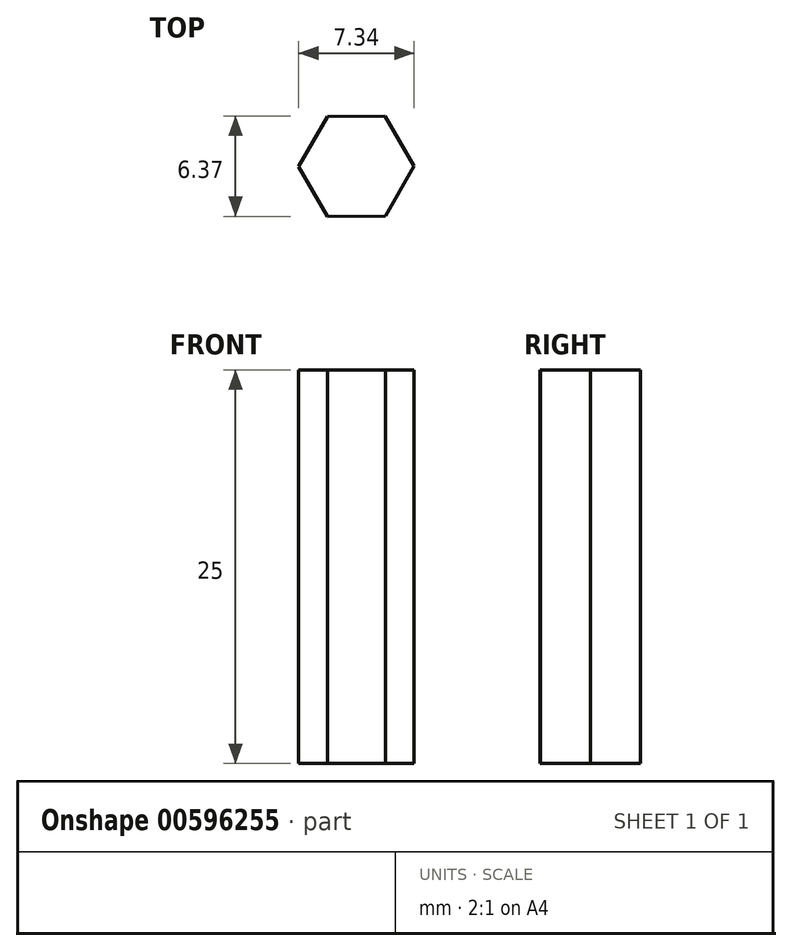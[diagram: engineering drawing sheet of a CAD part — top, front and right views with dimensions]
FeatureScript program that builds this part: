
annotation { "Feature Type Name" : "Feature", "Feature Type Description" : "" }
export const myFeature = defineFeature(function(context is Context, id is Id, definition is map)
    precondition{}
    {
        {
            var Q0;
            Q0=qCreatedBy(makeId("Top.planeOp"),FACE);
            var sketch = newSketch(context, id + "F0", { "sketchPlane" : qUnion([Q0])});
            skCircle(sketch, "E0.cCircle", {"center": v(0, 0) * mm, "radius": 3.18 * mm, "construction": true});
            skLineSegment(sketch, "E0.0", {"start": v(-1.83, -3.2) * mm, "end": v(-3.68, -0.02) * mm});
            skLineSegment(sketch, "E0.1", {"start": v(-3.68, -0.02) * mm, "end": v(-1.85, 3.16) * mm});
            skLineSegment(sketch, "E0.2", {"start": v(-1.85, 3.16) * mm, "end": v(1.81, 3.18) * mm});
            skLineSegment(sketch, "E0.3", {"start": v(1.81, 3.18) * mm, "end": v(3.66, 0) * mm});
            skLineSegment(sketch, "E0.4", {"start": v(3.66, 0) * mm, "end": v(1.84, -3.18) * mm});
            skLineSegment(sketch, "E0.5", {"start": v(1.84, -3.18) * mm, "end": v(-1.83, -3.2) * mm});
            skPoint(sketch, "E0.0.midPoint", {"position": v(-2.75, -1.6) * mm});
            skSolve(sketch);
        }
        {
            var Q0;
            Q0 = qSketchRegion(id + "F0", true);
            var Q1;
            Q1 = qConstructionFilter(qBodyType(qCreatedBy(id + "F0" ,EDGE), BodyType.WIRE), ConstructionObject.NO);
            extrude(context, id + "F1", {"entities" : qUnion([Q0]), "surfaceEntities" : qUnion([Q1]), "depth" : 25 * mm, "offsetDistance" : 25 * mm});
        }
    });
